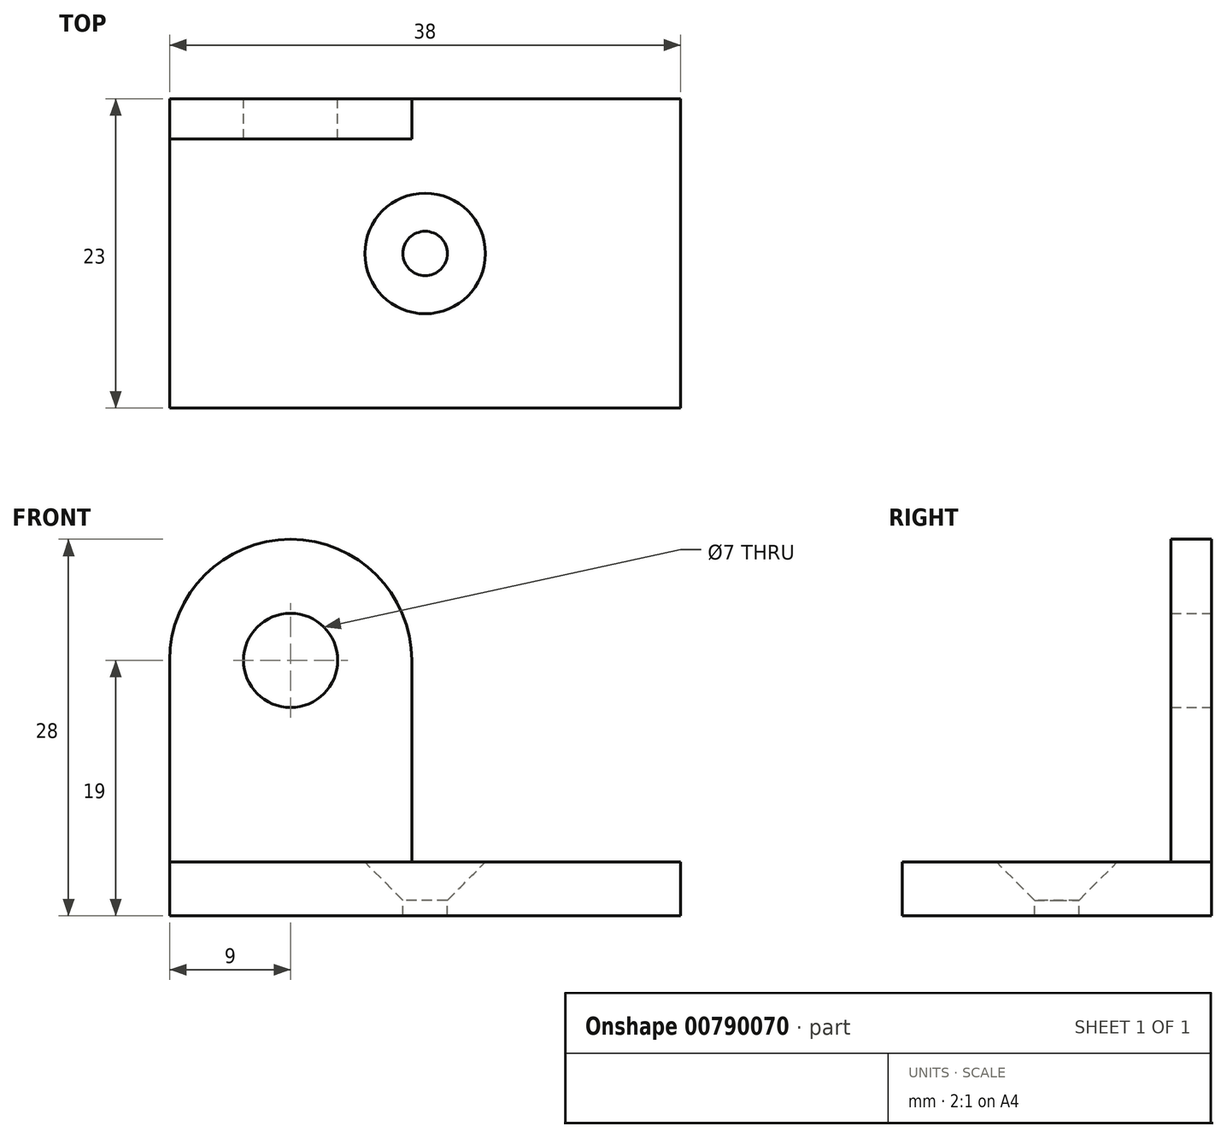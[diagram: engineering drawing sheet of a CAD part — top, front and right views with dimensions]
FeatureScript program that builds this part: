
annotation { "Feature Type Name" : "Feature", "Feature Type Description" : "" }
export const myFeature = defineFeature(function(context is Context, id is Id, definition is map)
    precondition{}
    {
        {
            var Q0;
            Q0=qCreatedBy(makeId("Front.planeOp"),FACE);
            var sketch = newSketch(context, id + "F0", { "sketchPlane" : qUnion([Q0])});
            skLineSegment(sketch, "E0", {"start": v(0, 0) * mm, "end": v(0, 19) * mm});
            skLineSegment(sketch, "E1", {"start": v(18, 19) * mm, "end": v(18, 4) * mm});
            skLineSegment(sketch, "E2", {"start": v(18, 4) * mm, "end": v(38, 4) * mm});
            skLineSegment(sketch, "E3", {"start": v(38, 4) * mm, "end": v(38, 0) * mm});
            skLineSegment(sketch, "E4", {"start": v(38, 0) * mm, "end": v(0, 0) * mm});
            skCircle(sketch, "E5", {"center": v(9, 19) * mm, "radius": 9 * mm});
            skCircle(sketch, "E6", {"center": v(9, 19) * mm, "radius": 3.5 * mm});
            skSolve(sketch);
        }
        {
            var Q0;
            Q0 = qSketchRegion(id + "F0", true);
            extrude(context, id + "F1", {"entities" : qUnion([Q0]), "depth" : 3 * mm, "offsetDistance" : 25 * mm});
        }
        {
            var Q0;
            Q0=makeQuery(id+"F1.opExtrude","CAP_FACE",FACE,{"disambiguationData":[OSD([sQuery(id+"F0.wireOp",EDGE,"E0"),sQuery(id+"F0.wireOp",EDGE,"E1"),sQuery(id+"F0.wireOp",EDGE,"E2"),sQuery(id+"F0.wireOp",EDGE,"E3"),sQuery(id+"F0.wireOp",EDGE,"E4"),sQuery(id+"F0.wireOp",EDGE,"E5"),sQuery(id+"F0.wireOp",EDGE,"E6")])],"isStart":false});
            var sketch = newSketch(context, id + "F2", { "sketchPlane" : qUnion([Q0])});
            skLineSegment(sketch, "E7.bottom", {"start": v(38, 0) * mm, "end": v(0, 0) * mm});
            skLineSegment(sketch, "E7.top", {"start": v(38, 4) * mm, "end": v(0, 4) * mm});
            skLineSegment(sketch, "E7.left", {"start": v(38, 0) * mm, "end": v(38, 4) * mm});
            skLineSegment(sketch, "E7.right", {"start": v(0, 0) * mm, "end": v(0, 4) * mm});
            skSolve(sketch);
        }
        {
            var Q0;
            Q0=makeQuery(id+"F2.imprint","IMPRINT",FACE,{"disambiguationData":[TD([[makeQuery(id+"F2.imprint","IMPRINT",EDGE,{"derivedFrom":sQuery(id+"F2.wireOp",EDGE,"E7.bottom")}),-1.0]])]});
            extrude(context, id + "F3", {"entities" : qUnion([Q0]), "operationType" : NewBodyOperationType.ADD, "depth" : 20 * mm, "offsetDistance" : 25 * mm});
        }
        {
            var Q0;
            Q0=makeQuery(id+"F3.boolean.opBoolean","MERGE",FACE,{"derivedFrom":[makeQuery(id+"F1.opExtrude","SWEPT_FACE",FACE,{"disambiguationData":[OSD([sQuery(id+"F0.wireOp",EDGE,"E2")])]}),makeQuery(id+"F3.opExtrude","SWEPT_FACE",FACE,{"disambiguationData":[OSD([sQuery(id+"F2.wireOp",EDGE,"E7.top")])]})]});
            var sketch = newSketch(context, id + "F4", { "sketchPlane" : qUnion([Q0])});
            skLineSegment(sketch, "E8", {"start": v(38, 0) * mm, "end": v(0, -23) * mm});
            skPoint(sketch, "E9", {"position": v(19, -11.5) * mm});
            skSolve(sketch);
        }
        {
            var Q0;
            Q0=sQuery(id+"F4.wireOp",VERTEX,"E9");
            var Q1;
            Q1=makeQuery(id+"F1.opExtrude","SWEPT_BODY",BODY,{"disambiguationData":[OSD([sQuery(id+"F0.wireOp",EDGE,"E0"),sQuery(id+"F0.wireOp",EDGE,"E1"),sQuery(id+"F0.wireOp",EDGE,"E2"),sQuery(id+"F0.wireOp",EDGE,"E3"),sQuery(id+"F0.wireOp",EDGE,"E4"),sQuery(id+"F0.wireOp",EDGE,"E5"),sQuery(id+"F0.wireOp",EDGE,"E6")])]});
            hole(context, id + "F5", {"style" : HoleStyle.C_SINK, "endStyle" : HoleEndStyle.THROUGH, "standardTappedOrClearance" : lookupTablePath({ "standard" : "ISO", "engagement" : "75%", "pitch" : "0.7 mm", "size" : "M4", "type" : "Tapped" }), "standardBlindInLast" : lookupTablePath({ "standard" : "ISO", "engagement" : "75%", "pitch" : "0.7 mm", "size" : "M4", "type" : "Tapped" }), "holeDiameter" : 3.3 * mm, "cSinkDiameter" : 8.96 * mm, "cSinkAngle" : 90 * degree, "majorDiameter" : 4 * mm, "showTappedDepth" : true, "isTappedThrough" : true, "tappedDepth" : 12 * mm, "tapClearance" : 3, "locations" : qUnion([Q0]), "scope" : qUnion([Q1])});
        }
    });
